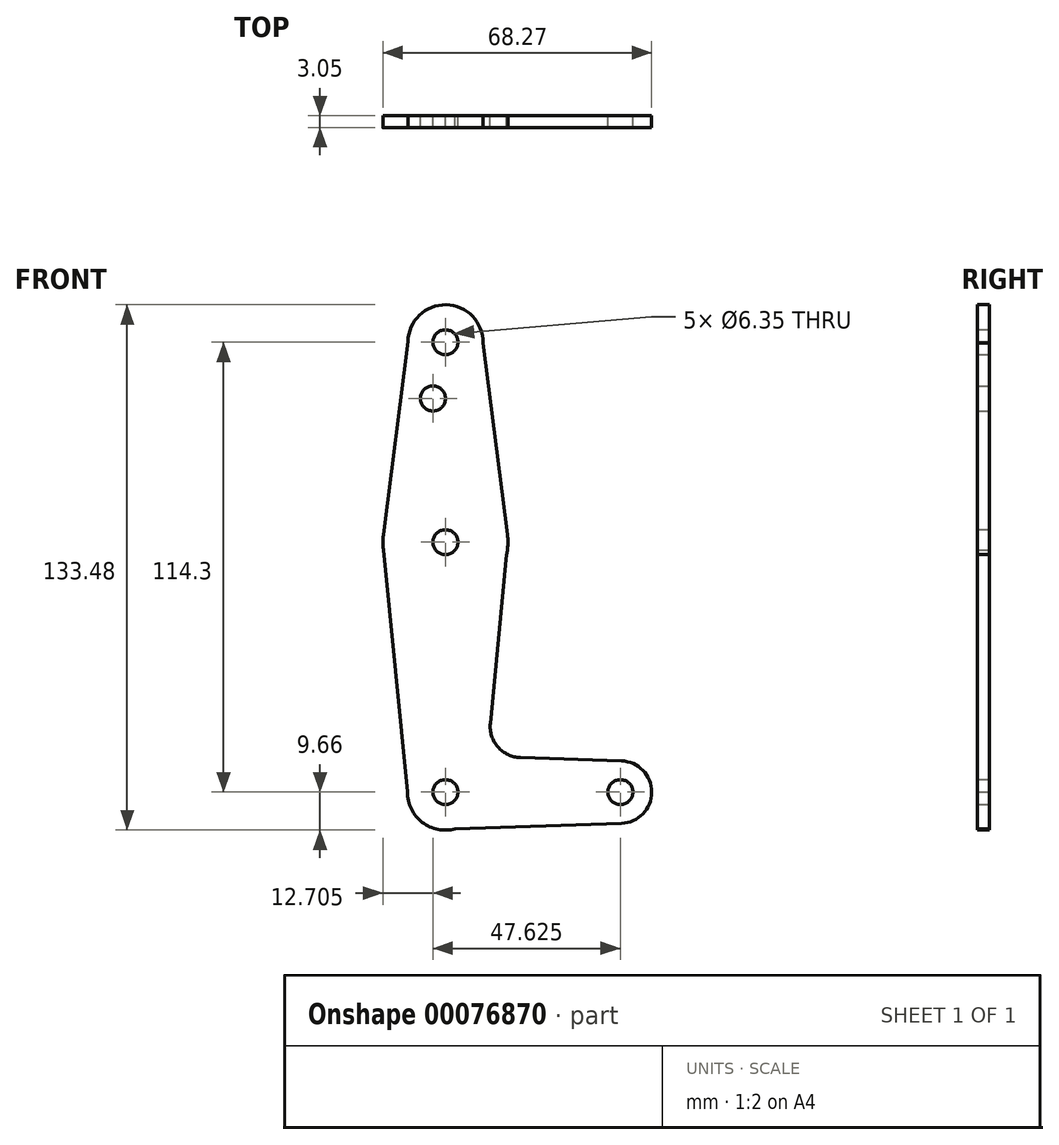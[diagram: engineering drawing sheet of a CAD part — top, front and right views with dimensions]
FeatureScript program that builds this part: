
annotation { "Feature Type Name" : "Feature", "Feature Type Description" : "" }
export const myFeature = defineFeature(function(context is Context, id is Id, definition is map)
    precondition{}
    {
        {
            var Q0;
            Q0=qCreatedBy(makeId("Front.planeOp"),FACE);
            var sketch = newSketch(context, id + "F0", { "sketchPlane" : qUnion([Q0])});
            skLineSegment(sketch, "E0", {"start": v(0, 0) * mm, "end": v(0, 114.3) * mm, "construction": true});
            skLineSegment(sketch, "E1", {"start": v(0, 0) * mm, "end": v(44.45, 0) * mm, "construction": true});
            skCircle(sketch, "E2", {"center": v(0, 114.3) * mm, "radius": 9.53 * mm});
            skCircle(sketch, "E3", {"center": v(0, 63.5) * mm, "radius": 15.88 * mm});
            skCircle(sketch, "E4", {"center": v(0, 0) * mm, "radius": 9.66 * mm});
            skCircle(sketch, "E5", {"center": v(44.45, 0) * mm, "radius": 7.94 * mm});
            skLineSegment(sketch, "E6", {"start": v(-9.52, 114.5) * mm, "end": v(-15.75, 65.5) * mm});
            skLineSegment(sketch, "E7", {"start": v(9.52, 114.13) * mm, "end": v(15.75, 65.52) * mm});
            skLineSegment(sketch, "E8", {"start": v(15.56, 60.36) * mm, "end": v(11.4, 17.49) * mm});
            skLineSegment(sketch, "E9", {"start": v(19.05, 8.77) * mm, "end": v(44.71, 7.93) * mm});
            skLineSegment(sketch, "E10", {"start": v(2.49, -9.33) * mm, "end": v(44.71, -7.93) * mm});
            skCircle(sketch, "E11", {"center": v(0, 114.3) * mm, "radius": 3.18 * mm});
            skCircle(sketch, "E12", {"center": v(0, 0) * mm, "radius": 3.18 * mm});
            skCircle(sketch, "E13", {"center": v(44.45, 0) * mm, "radius": 3.18 * mm});
            skCircle(sketch, "E14", {"center": v(0, 63.5) * mm, "radius": 3.18 * mm});
            skCircle(sketch, "E15", {"center": v(-3.18, 100.03) * mm, "radius": 3.18 * mm});
            skArc(sketch, "E16.filletArc", {"start": v(11.4, 17.49) * mm, "mid": v(13.34, 11.47) * mm, "end": v(19.05, 8.77) * mm});
            skLineSegment(sketch, "E17", {"start": v(-9.66, 0) * mm, "end": v(-15.75, 61.5) * mm});
            skSolve(sketch);
        }
        {
            var Q0;
            Q0 = qSketchRegion(id + "F0", true);
            extrude(context, id + "F1", {"entities" : qUnion([Q0]), "depth" : 3.05 * mm});
        }
    });
